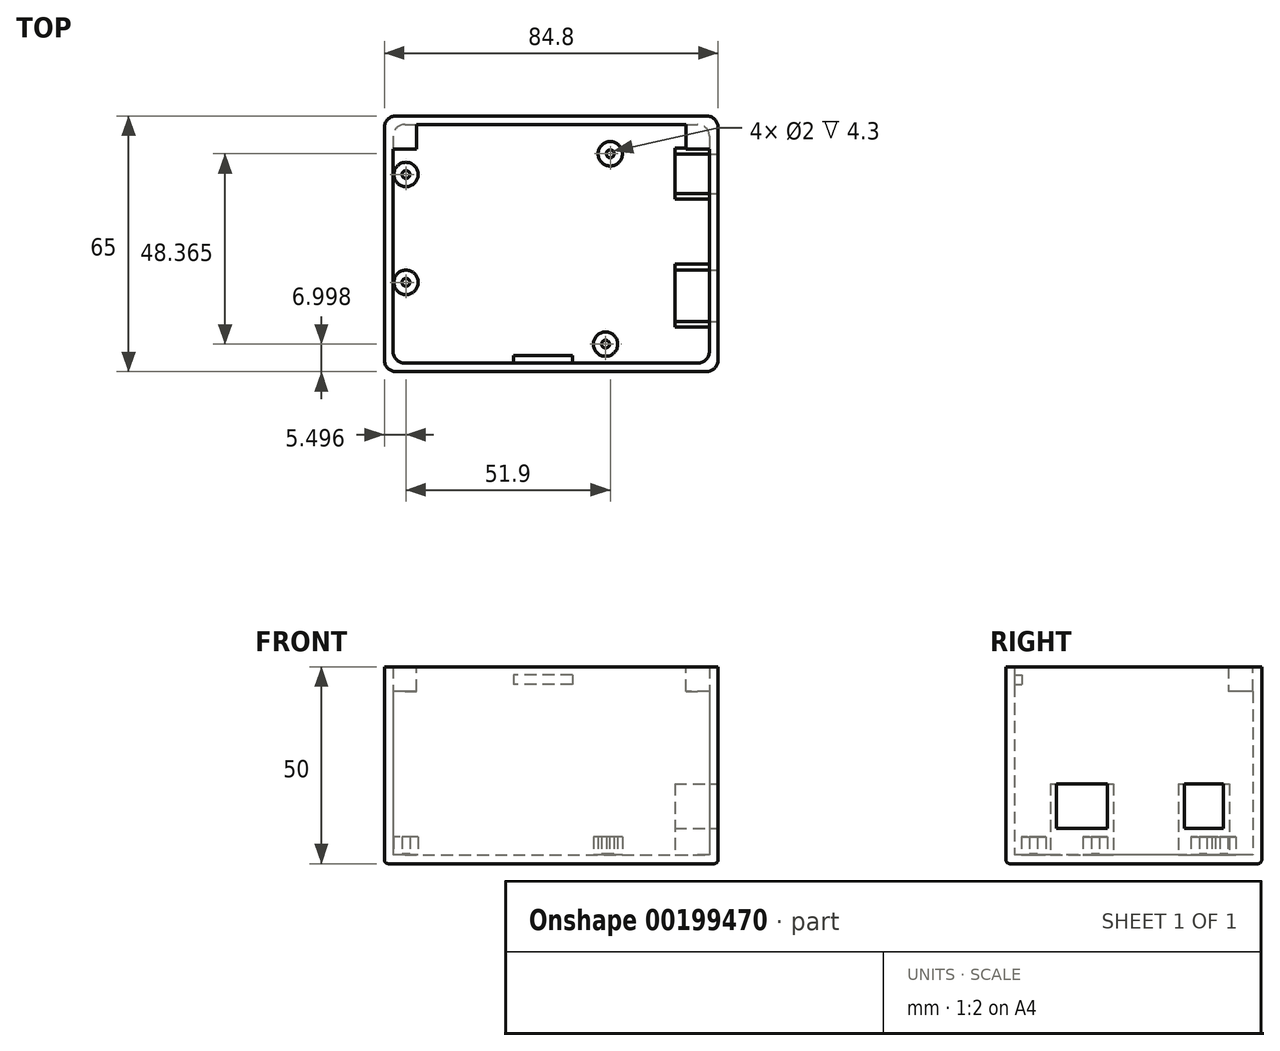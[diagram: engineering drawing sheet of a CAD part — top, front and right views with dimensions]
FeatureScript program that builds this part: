
annotation { "Feature Type Name" : "Feature", "Feature Type Description" : "" }
export const myFeature = defineFeature(function(context is Context, id is Id, definition is map)
    precondition{}
    {
        {
            var Q0;
            Q0=qCreatedBy(makeId("Top.planeOp"),FACE);
            var sketch = newSketch(context, id + "F0", { "sketchPlane" : qUnion([Q0])});
            skLineSegment(sketch, "E0.bottom", {"start": v(-75.5, 23.49) * mm, "end": v(9.3, 23.49) * mm});
            skLineSegment(sketch, "E0.top", {"start": v(-75.5, -41.51) * mm, "end": v(9.3, -41.51) * mm});
            skLineSegment(sketch, "E0.left", {"start": v(-75.5, 23.49) * mm, "end": v(-75.5, -41.51) * mm});
            skLineSegment(sketch, "E0.right", {"start": v(9.3, 23.49) * mm, "end": v(9.3, -41.51) * mm});
            skCircle(sketch, "E1", {"center": v(-70, 8.59) * mm, "radius": 3.1 * mm});
            skCircle(sketch, "E2", {"center": v(-70, -18.81) * mm, "radius": 3.1 * mm});
            skCircle(sketch, "E3", {"center": v(-19.3, -34.51) * mm, "radius": 3.1 * mm});
            skCircle(sketch, "E4", {"center": v(-18.1, 13.85) * mm, "radius": 3.1 * mm});
            skCircle(sketch, "E5", {"center": v(-70, 8.59) * mm, "radius": 1 * mm});
            skCircle(sketch, "E6", {"center": v(-18.1, 13.85) * mm, "radius": 1 * mm});
            skCircle(sketch, "E7", {"center": v(-70, -18.81) * mm, "radius": 1 * mm});
            skCircle(sketch, "E8", {"center": v(-19.3, -34.51) * mm, "radius": 1 * mm});
            skLineSegment(sketch, "E9.bottom", {"start": v(-65.5, -41.51) * mm, "end": v(-0.7, -41.51) * mm});
            skLineSegment(sketch, "E10.bottom", {"start": v(-38.1, -34.31) * mm, "end": v(-28.1, -34.31) * mm});
            skLineSegment(sketch, "E10.top", {"start": v(-38.1, -39.31) * mm, "end": v(-28.1, -39.31) * mm});
            skLineSegment(sketch, "E10.left", {"start": v(-38.1, -34.31) * mm, "end": v(-38.1, -39.31) * mm});
            skLineSegment(sketch, "E10.right", {"start": v(-28.1, -34.31) * mm, "end": v(-28.1, -39.31) * mm});
            skSolve(sketch);
        }
        {
            var Q0;
            Q0=makeQuery(id+"F0.imprint","IMPRINT",FACE,{"disambiguationData":[TD([[makeQuery(id+"F0.imprint","IMPRINT",EDGE,{"derivedFrom":sQuery(id+"F0.wireOp",EDGE,"E0.bottom")}),-1.0]])]});
            var Q1;
            Q1=makeQuery(id+"F0.imprint","IMPRINT",FACE,{"disambiguationData":[TD([[makeQuery(id+"F0.imprint","IMPRINT",EDGE,{"derivedFrom":sQuery(id+"F0.wireOp",EDGE,"E2")}),1.0]])]});
            var Q2;
            Q2=makeQuery(id+"F0.imprint","IMPRINT",FACE,{"disambiguationData":[TD([[makeQuery(id+"F0.imprint","IMPRINT",EDGE,{"derivedFrom":sQuery(id+"F0.wireOp",EDGE,"E1")}),1.0]])]});
            var Q3;
            Q3=makeQuery(id+"F0.imprint","IMPRINT",FACE,{"disambiguationData":[TD([[makeQuery(id+"F0.imprint","IMPRINT",EDGE,{"derivedFrom":sQuery(id+"F0.wireOp",EDGE,"E4")}),1.0]])]});
            var Q4;
            Q4=makeQuery(id+"F0.imprint","IMPRINT",FACE,{"disambiguationData":[TD([[makeQuery(id+"F0.imprint","IMPRINT",EDGE,{"derivedFrom":sQuery(id+"F0.wireOp",EDGE,"E3")}),1.0]])]});
            var Q5;
            Q5=makeQuery(id+"F0.imprint","IMPRINT",FACE,{"disambiguationData":[TD([[makeQuery(id+"F0.imprint","IMPRINT",EDGE,{"derivedFrom":sQuery(id+"F0.wireOp",EDGE,"VA1Hmh23-WBGZ-7FsX-Ouzs-l9uVdtuXwfrv.bottom")}),1.0]])]});
            var Q6;
            Q6=makeQuery(id+"F0.imprint","IMPRINT",FACE,{"disambiguationData":[TD([[makeQuery(id+"F0.imprint","IMPRINT",EDGE,{"derivedFrom":sQuery(id+"F0.wireOp",EDGE,"E10.bottom")}),-1.0]])]});
            extrude(context, id + "F1", {"entities" : qUnion([Q0, Q1, Q2, Q3, Q4, Q5, Q6]), "depth" : 50 * mm});
        }
        {
            var Q0;
            Q0=makeQuery(id+"F1.opExtrude","SWEPT_FACE",FACE,{"disambiguationData":[OSD([sQuery(id+"F0.wireOp",EDGE,"E2")])]});
            var Q1;
            Q1=makeQuery(id+"F1.opExtrude","SWEPT_FACE",FACE,{"disambiguationData":[OSD([sQuery(id+"F0.wireOp",EDGE,"E1")])]});
            var Q2;
            Q2=makeQuery(id+"F1.opExtrude","SWEPT_FACE",FACE,{"disambiguationData":[OSD([sQuery(id+"F0.wireOp",EDGE,"E4")])]});
            var Q3;
            Q3=makeQuery(id+"F1.opExtrude","SWEPT_FACE",FACE,{"disambiguationData":[OSD([sQuery(id+"F0.wireOp",EDGE,"E3")])]});
            var Q4;
            Q4=makeQuery(id+"F1.opExtrude","SWEPT_FACE",FACE,{"disambiguationData":[OSD([sQuery(id+"F0.wireOp",EDGE,"E7")])]});
            var Q5;
            Q5=makeQuery(id+"F1.opExtrude","SWEPT_FACE",FACE,{"disambiguationData":[OSD([sQuery(id+"F0.wireOp",EDGE,"E5")])]});
            var Q6;
            Q6=makeQuery(id+"F1.opExtrude","SWEPT_FACE",FACE,{"disambiguationData":[OSD([sQuery(id+"F0.wireOp",EDGE,"E8")])]});
            var Q7;
            Q7=makeQuery(id+"F1.opExtrude","SWEPT_FACE",FACE,{"disambiguationData":[OSD([sQuery(id+"F0.wireOp",EDGE,"E6")])]});
            var Q8;
            Q8=makeQuery(id+"F1.opExtrude","CAP_FACE",FACE,{"disambiguationData":[OSD([sQuery(id+"F0.wireOp",EDGE,"E0.bottom"),sQuery(id+"F0.wireOp",EDGE,"E0.left"),sQuery(id+"F0.wireOp",EDGE,"7W9O8lOB-wSMZ-6HX8-2Pzd-baJFNFpb0Sld")])],"isStart":false});
            var Q9;
            Q9=makeQuery(id+"F1.opExtrude","CAP_FACE",FACE,{"disambiguationData":[OSD([sQuery(id+"F0.wireOp",EDGE,"E0.bottom"),sQuery(id+"F0.wireOp",EDGE,"E0.right"),sQuery(id+"F0.wireOp",EDGE,"6wA7PAN0-a5WZ-xzTv-JZU7-1fsM9sgV2JZ6")])],"isStart":false});
            var Q10;
            Q10=makeQuery(id+"F1.opExtrude","SWEPT_FACE",FACE,{"disambiguationData":[OSD([sQuery(id+"F0.wireOp",EDGE,"u36fmcnV-SRn1-kItR-ujeD-uHerwh8gpMvl")])]});
            shell(context, id + "F2", {"entities" : qUnion([Q0, Q1, Q2, Q3, Q4, Q5, Q6, Q7, Q8, Q9, Q10]), "thickness" : 2.2 * mm});
        }
        {
            var Q0;
            Q0=makeQuery(id+"F1.opExtrude","SWEPT_FACE",FACE,{"disambiguationData":[OSD([sQuery(id+"F0.wireOp",EDGE,"E0.right")])]});
            var sketch = newSketch(context, id + "F3", { "sketchPlane" : qUnion([Q0])});
            skLineSegment(sketch, "E11.bottom", {"start": v(-28.71, 20.3) * mm, "end": v(-15.71, 20.3) * mm});
            skLineSegment(sketch, "E11.top", {"start": v(-28.71, 9) * mm, "end": v(-15.71, 9) * mm});
            skLineSegment(sketch, "E11.left", {"start": v(-28.71, 20.3) * mm, "end": v(-28.71, 9) * mm});
            skLineSegment(sketch, "E11.right", {"start": v(-15.71, 20.3) * mm, "end": v(-15.71, 9) * mm});
            skLineSegment(sketch, "E12.bottom", {"start": v(3.79, 20.3) * mm, "end": v(13.79, 20.3) * mm});
            skLineSegment(sketch, "E12.top", {"start": v(3.79, 9) * mm, "end": v(13.79, 9) * mm});
            skLineSegment(sketch, "E12.left", {"start": v(3.79, 20.3) * mm, "end": v(3.79, 9) * mm});
            skLineSegment(sketch, "E12.right", {"start": v(13.79, 20.3) * mm, "end": v(13.79, 9) * mm});
            skLineSegment(sketch, "E13.bottom", {"start": v(-30.21, 20.3) * mm, "end": v(-14.21, 20.3) * mm});
            skLineSegment(sketch, "E13.top", {"start": v(-30.21, 0) * mm, "end": v(-14.21, 0) * mm});
            skLineSegment(sketch, "E13.left", {"start": v(-30.21, 20.3) * mm, "end": v(-30.21, 0) * mm});
            skLineSegment(sketch, "E13.right", {"start": v(-14.21, 20.3) * mm, "end": v(-14.21, 0) * mm});
            skLineSegment(sketch, "E14.bottom", {"start": v(2.29, 20.3) * mm, "end": v(15.29, 20.3) * mm});
            skLineSegment(sketch, "E14.top", {"start": v(2.29, 0) * mm, "end": v(15.29, 0) * mm});
            skLineSegment(sketch, "E14.left", {"start": v(2.29, 20.3) * mm, "end": v(2.29, 0) * mm});
            skLineSegment(sketch, "E14.right", {"start": v(15.29, 20.3) * mm, "end": v(15.29, 0) * mm});
            skSolve(sketch);
        }
        {
            var Q0;
            {var subQ1=sQuery(id+"F3.wireOp",EDGE,"E11.top");Q0=makeQuery(id+"F3.imprint","IMPRINT",FACE,{"disambiguationData":[TD([[makeQuery(id+"F3.imprint","IMPRINT",EDGE,{"derivedFrom":subQ1}),-1.0]])]});}
            var Q1;
            Q1=makeQuery(id+"F3.imprint","IMPRINT",FACE,{"disambiguationData":[TD([[makeQuery(id+"F3.imprint","IMPRINT",EDGE,{"derivedFrom":sQuery(id+"F3.wireOp",EDGE,"E12.top")}),-1.0]])]});
            extrude(context, id + "F4", {"entities" : qUnion([Q0, Q1]), "operationType" : NewBodyOperationType.ADD, "oppositeDirection" : true, "depth" : 11 * mm});
        }
        {
            var Q0;
            {var subQ0=sQuery(id+"F3.wireOp",EDGE,"E11.top");Q0=makeQuery(id+"F3.imprint","IMPRINT",FACE,{"disambiguationData":[TD([[makeQuery(id+"F3.imprint","IMPRINT",EDGE,{"derivedFrom":subQ0}),1.0]])]});}
            extrude(context, id + "F5", {"entities" : qUnion([Q0]), "operationType" : NewBodyOperationType.REMOVE, "oppositeDirection" : true, "depth" : 12 * mm});
        }
        {
            var Q0;
            Q0=makeQuery(id+"F3.imprint","IMPRINT",FACE,{"disambiguationData":[TD([[makeQuery(id+"F3.imprint","IMPRINT",EDGE,{"derivedFrom":sQuery(id+"F3.wireOp",EDGE,"E12.top")}),1.0]])]});
            extrude(context, id + "F6", {"entities" : qUnion([Q0]), "operationType" : NewBodyOperationType.REMOVE, "oppositeDirection" : true, "depth" : 25 * mm});
        }
        {
            var Q0;
            Q0=makeQuery(id+"F1.opExtrude","SWEPT_EDGE",EDGE,{"disambiguationData":[OSD([sQuery(id+"F0.wireOp",EDGE,"E0.top"),sQuery(id+"F0.wireOp",EDGE,"E0.right")])]});
            var Q1;
            Q1=makeQuery(id+"F1.opExtrude","SWEPT_EDGE",EDGE,{"disambiguationData":[OSD([sQuery(id+"F0.wireOp",EDGE,"E0.bottom"),sQuery(id+"F0.wireOp",EDGE,"E0.right")])]});
            var Q2;
            Q2=makeQuery(id+"F1.opExtrude","SWEPT_EDGE",EDGE,{"disambiguationData":[OSD([sQuery(id+"F0.wireOp",EDGE,"E0.bottom"),sQuery(id+"F0.wireOp",EDGE,"E0.left")])]});
            var Q3;
            Q3=makeQuery(id+"F1.opExtrude","SWEPT_EDGE",EDGE,{"disambiguationData":[OSD([sQuery(id+"F0.wireOp",EDGE,"E0.top"),sQuery(id+"F0.wireOp",EDGE,"E0.left")])]});
            var Q4;
            Q4=makeQuery(id+"F2.opShell","OFFSET_EDGE",EDGE,{"disambiguationData":[OSD([sQuery(id+"F0.wireOp",EDGE,"E0.bottom"),sQuery(id+"F0.wireOp",EDGE,"E0.right")])]});
            var Q5;
            Q5=makeQuery(id+"F2.opShell","OFFSET_EDGE",EDGE,{"disambiguationData":[OSD([sQuery(id+"F0.wireOp",EDGE,"E0.top"),sQuery(id+"F0.wireOp",EDGE,"E0.right")])]});
            var Q6;
            Q6=makeQuery(id+"F2.opShell","OFFSET_EDGE",EDGE,{"disambiguationData":[OSD([sQuery(id+"F0.wireOp",EDGE,"E0.top"),sQuery(id+"F0.wireOp",EDGE,"E0.left")])]});
            var Q7;
            Q7=makeQuery(id+"F2.opShell","OFFSET_EDGE",EDGE,{"disambiguationData":[OSD([sQuery(id+"F0.wireOp",EDGE,"E0.bottom"),sQuery(id+"F0.wireOp",EDGE,"E0.left")])]});
            fillet(context, id + "F7", {"entities" : qUnion([Q0, Q1, Q2, Q3, Q4, Q5, Q6, Q7]), "radius" : 3 * mm, "tangentPropagation" : true, "allowEdgeOverflow" : false});
        }
        {
            var Q0;
            Q0=makeQuery(id+"F1.opExtrude","SWEPT_FACE",FACE,{"disambiguationData":[OSD([sQuery(id+"F0.wireOp",EDGE,"E0.left")])]});
            var sketch = newSketch(context, id + "F8", { "sketchPlane" : qUnion([Q0])});
            skLineSegment(sketch, "E15.bottom", {"start": v(-11.09, 45) * mm, "end": v(-3.09, 45) * mm});
            skLineSegment(sketch, "E15.top", {"start": v(-11.09, 42) * mm, "end": v(-3.09, 42) * mm});
            skLineSegment(sketch, "E15.left", {"start": v(-11.09, 45) * mm, "end": v(-11.09, 42) * mm});
            skLineSegment(sketch, "E15.right", {"start": v(-3.09, 45) * mm, "end": v(-3.09, 42) * mm});
            skLineSegment(sketch, "E16.bottom", {"start": v(19.21, 45) * mm, "end": v(27.21, 45) * mm});
            skLineSegment(sketch, "E16.top", {"start": v(19.21, 42) * mm, "end": v(27.21, 42) * mm});
            skLineSegment(sketch, "E16.left", {"start": v(19.21, 45) * mm, "end": v(19.21, 42) * mm});
            skLineSegment(sketch, "E16.right", {"start": v(27.21, 45) * mm, "end": v(27.21, 42) * mm});
            skSolve(sketch);
        }
        {
            var Q0;
            Q0=makeQuery(id+"F0.imprint","IMPRINT",FACE,{"disambiguationData":[TD([[makeQuery(id+"F0.imprint","IMPRINT",EDGE,{"derivedFrom":sQuery(id+"F0.wireOp",EDGE,"E1")}),1.0]])]});
            var Q1;
            Q1=makeQuery(id+"F0.imprint","IMPRINT",FACE,{"disambiguationData":[TD([[makeQuery(id+"F0.imprint","IMPRINT",EDGE,{"derivedFrom":sQuery(id+"F0.wireOp",EDGE,"E4")}),1.0]])]});
            var Q2;
            Q2=makeQuery(id+"F0.imprint","IMPRINT",FACE,{"disambiguationData":[TD([[makeQuery(id+"F0.imprint","IMPRINT",EDGE,{"derivedFrom":sQuery(id+"F0.wireOp",EDGE,"E2")}),1.0]])]});
            var Q3;
            Q3=makeQuery(id+"F0.imprint","IMPRINT",FACE,{"disambiguationData":[TD([[makeQuery(id+"F0.imprint","IMPRINT",EDGE,{"derivedFrom":sQuery(id+"F0.wireOp",EDGE,"E3")}),1.0]])]});
            var Q4;
            Q4=sQuery(id+"F0.wireOp",EDGE,"E4");
            var Q5;
            Q5=sQuery(id+"F0.wireOp",EDGE,"E3");
            var Q6;
            Q6=sQuery(id+"F0.wireOp",EDGE,"E1");
            var Q7;
            Q7=sQuery(id+"F0.wireOp",EDGE,"E2");
            extrude(context, id + "F9", {"entities" : qUnion([Q0, Q1, Q2, Q3]), "operationType" : NewBodyOperationType.ADD, "surfaceEntities" : qUnion([Q4, Q5, Q6, Q7]), "depth" : 6.8 * mm});
        }
        {
            var Q0;
            Q0=makeQuery(id+"F0.imprint","IMPRINT",FACE,{"disambiguationData":[TD([[makeQuery(id+"F0.imprint","IMPRINT",EDGE,{"derivedFrom":sQuery(id+"F0.wireOp",EDGE,"E6")}),1.0]])]});
            var Q1;
            Q1=makeQuery(id+"F0.imprint","IMPRINT",FACE,{"disambiguationData":[TD([[makeQuery(id+"F0.imprint","IMPRINT",EDGE,{"derivedFrom":sQuery(id+"F0.wireOp",EDGE,"E1")}),1.0]])]});
            var Q2;
            Q2=makeQuery(id+"F0.imprint","IMPRINT",FACE,{"disambiguationData":[TD([[makeQuery(id+"F0.imprint","IMPRINT",EDGE,{"derivedFrom":sQuery(id+"F0.wireOp",EDGE,"E7")}),1.0]])]});
            var Q3;
            Q3=makeQuery(id+"F0.imprint","IMPRINT",FACE,{"disambiguationData":[TD([[makeQuery(id+"F0.imprint","IMPRINT",EDGE,{"derivedFrom":sQuery(id+"F0.wireOp",EDGE,"E8")}),1.0]])]});
            var Q4;
            Q4=makeQuery(id+"F0.imprint","IMPRINT",FACE,{"disambiguationData":[TD([[makeQuery(id+"F0.imprint","IMPRINT",EDGE,{"derivedFrom":sQuery(id+"F0.wireOp",EDGE,"E5")}),1.0]])]});
            extrude(context, id + "F10", {"entities" : qUnion([Q0, Q1, Q2, Q3, Q4]), "operationType" : NewBodyOperationType.ADD, "depth" : 2.5 * mm});
        }
        {
            var Q0;
            {var subQ0=sQuery(id+"F0.wireOp",EDGE,"E8");var subQ1=sQuery(id+"F0.wireOp",EDGE,"E7");var subQ2=sQuery(id+"F0.wireOp",EDGE,"E6");Q0=makeQuery(id+"F10.boolean.opBoolean","MERGE",FACE,{"derivedFrom":[makeQuery(id+"F1.opExtrude","CAP_FACE",FACE,{"disambiguationData":[OSD([sQuery(id+"F0.wireOp",EDGE,"E0.bottom"),sQuery(id+"F0.wireOp",EDGE,"E0.top"),sQuery(id+"F0.wireOp",EDGE,"E0.left"),sQuery(id+"F0.wireOp",EDGE,"E0.right"),sQuery(id+"F0.wireOp",EDGE,"E5"),subQ2,subQ1,subQ0,sQuery(id+"F0.wireOp",EDGE,"E9.bottom")])],"isStart":true}),makeQuery(id+"F10.opExtrude","CAP_FACE",FACE,{"disambiguationData":[OSD([sQuery(id+"F0.wireOp",EDGE,"E1")])],"isStart":true}),makeQuery(id+"F10.opExtrude","CAP_FACE",FACE,{"disambiguationData":[OSD([subQ2])],"isStart":true}),makeQuery(id+"F10.opExtrude","CAP_FACE",FACE,{"disambiguationData":[OSD([subQ1])],"isStart":true}),makeQuery(id+"F10.opExtrude","CAP_FACE",FACE,{"disambiguationData":[OSD([subQ0])],"isStart":true})]});}
            fillet(context, id + "F11", {"entities" : qUnion([Q0]), "radius" : 1 * mm, "tangentPropagation" : true, "allowEdgeOverflow" : false});
        }
        {
            var Q0;
            Q0=qCreatedBy(makeId("Front.planeOp"),FACE);
            var sketch = newSketch(context, id + "F12", { "sketchPlane" : qUnion([Q0])});
            skLineSegment(sketch, "E17.bottom", {"start": v(7.1, 50) * mm, "end": v(1.1, 50) * mm});
            skLineSegment(sketch, "E17.top", {"start": v(7.1, 43.8) * mm, "end": v(1.1, 43.8) * mm});
            skLineSegment(sketch, "E17.left", {"start": v(7.1, 50) * mm, "end": v(7.1, 43.8) * mm});
            skLineSegment(sketch, "E17.right", {"start": v(1.1, 50) * mm, "end": v(1.1, 43.8) * mm});
            skLineSegment(sketch, "E18.bottom", {"start": v(-67.3, 50) * mm, "end": v(-73.3, 50) * mm});
            skLineSegment(sketch, "E18.top", {"start": v(-67.3, 43.8) * mm, "end": v(-73.3, 43.8) * mm});
            skLineSegment(sketch, "E18.left", {"start": v(-67.3, 50) * mm, "end": v(-67.3, 43.8) * mm});
            skLineSegment(sketch, "E18.right", {"start": v(-73.3, 50) * mm, "end": v(-73.3, 43.8) * mm});
            skSolve(sketch);
        }
        {
            var Q0;
            Q0=makeQuery(id+"F12.imprint","IMPRINT",FACE,{"disambiguationData":[TD([[makeQuery(id+"F12.imprint","IMPRINT",EDGE,{"derivedFrom":sQuery(id+"F12.wireOp",EDGE,"E17.bottom")}),1.0]])]});
            var Q1;
            Q1=makeQuery(id+"F12.imprint","IMPRINT",FACE,{"disambiguationData":[TD([[makeQuery(id+"F12.imprint","IMPRINT",EDGE,{"derivedFrom":sQuery(id+"F12.wireOp",EDGE,"E18.bottom")}),1.0]])]});
            extrude(context, id + "F13", {"entities" : qUnion([Q0, Q1]), "operationType" : NewBodyOperationType.ADD, "oppositeDirection" : true, "depth" : 21.3 * mm, "hasSecondDirection" : true, "secondDirectionOppositeDirection" : true, "secondDirectionDepth" : 15 * mm});
        }
        {
            var Q0;
            Q0=qCreatedBy(makeId("Front.planeOp"),FACE);
            var sketch = newSketch(context, id + "F14", { "sketchPlane" : qUnion([Q0])});
            skLineSegment(sketch, "E19.bottom", {"start": v(-27.7, 48) * mm, "end": v(-42.7, 48) * mm});
            skLineSegment(sketch, "E19.top", {"start": v(-27.7, 45.5) * mm, "end": v(-42.7, 45.5) * mm});
            skLineSegment(sketch, "E19.left", {"start": v(-27.7, 48) * mm, "end": v(-27.7, 45.5) * mm});
            skLineSegment(sketch, "E19.right", {"start": v(-42.7, 48) * mm, "end": v(-42.7, 45.5) * mm});
            skLineSegment(sketch, "E20.top", {"start": v(-27.7, 50) * mm, "end": v(-42.7, 50) * mm});
            skLineSegment(sketch, "E20.left", {"start": v(-27.7, 48) * mm, "end": v(-27.7, 50) * mm});
            skLineSegment(sketch, "E20.right", {"start": v(-42.7, 48) * mm, "end": v(-42.7, 50) * mm});
            skLineSegment(sketch, "E21.top", {"start": v(-27.7, 43.5) * mm, "end": v(-42.7, 43.5) * mm});
            skLineSegment(sketch, "E21.left", {"start": v(-27.7, 45.5) * mm, "end": v(-27.7, 43.5) * mm});
            skLineSegment(sketch, "E21.right", {"start": v(-42.7, 45.5) * mm, "end": v(-42.7, 43.5) * mm});
            skSolve(sketch);
        }
        {
            var Q0;
            Q0=makeQuery(id+"F14.imprint","IMPRINT",FACE,{"disambiguationData":[TD([[makeQuery(id+"F14.imprint","IMPRINT",EDGE,{"derivedFrom":sQuery(id+"F14.wireOp",EDGE,"E19.left")}),-1.0]])]});
            extrude(context, id + "F15", {"entities" : qUnion([Q0]), "operationType" : NewBodyOperationType.ADD, "depth" : 39.6 * mm, "hasSecondDirection" : true, "secondDirectionOppositeDirection" : false, "secondDirectionDepth" : 37.4 * mm});
        }
    });
